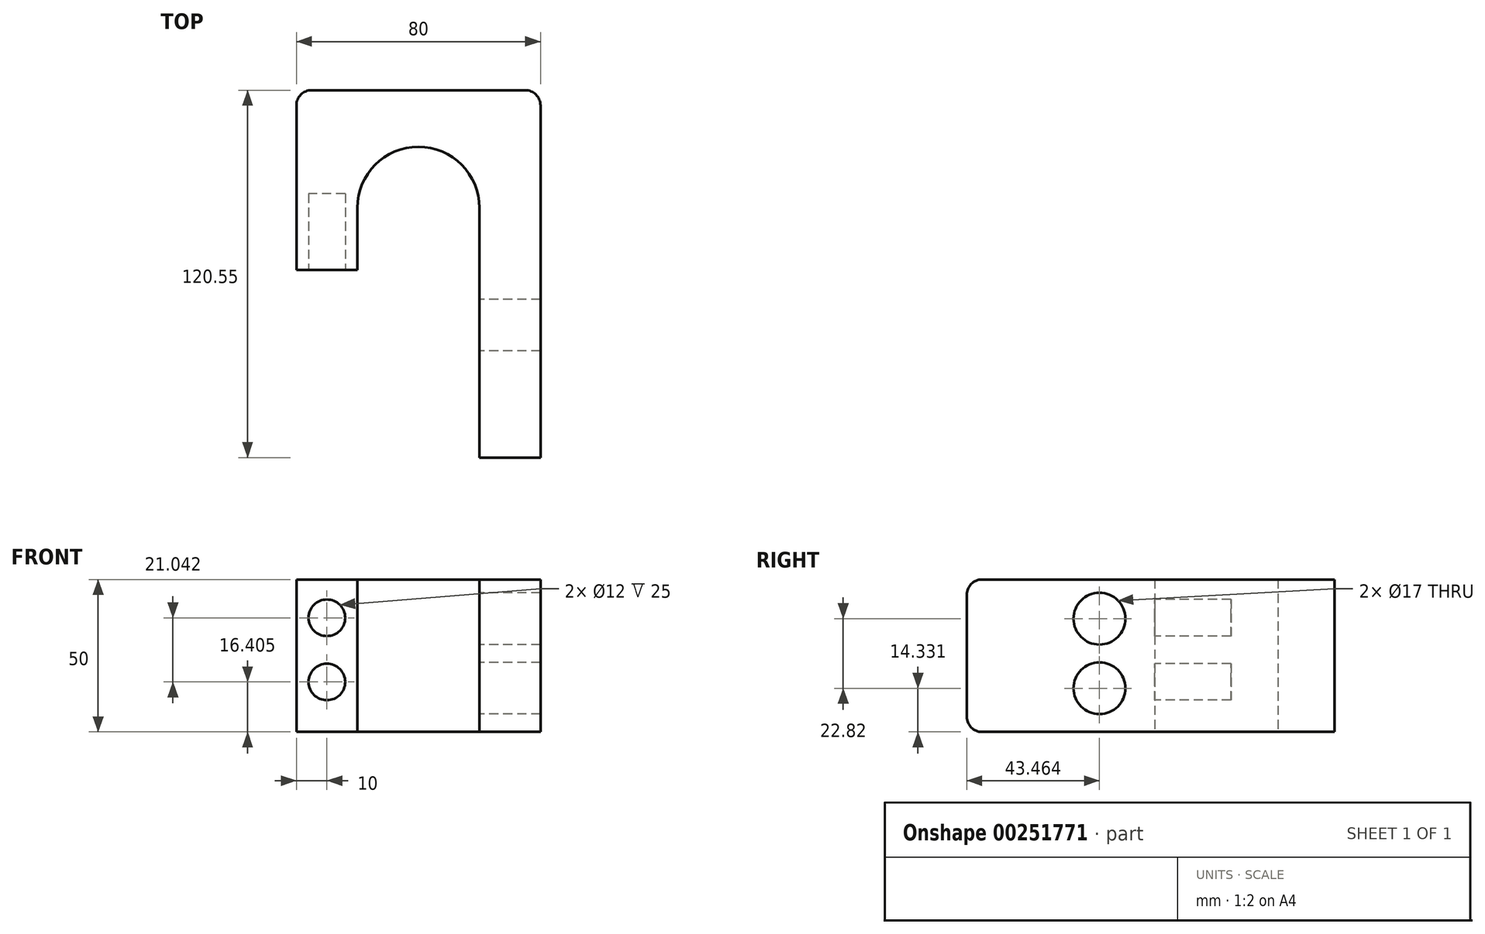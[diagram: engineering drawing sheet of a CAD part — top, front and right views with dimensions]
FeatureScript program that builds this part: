
annotation { "Feature Type Name" : "Feature", "Feature Type Description" : "" }
export const myFeature = defineFeature(function(context is Context, id is Id, definition is map)
    precondition{}
    {
        {
            var Q0;
            Q0=qCreatedBy(makeId("Top.planeOp"),FACE);
            var sketch = newSketch(context, id + "F0", { "sketchPlane" : qUnion([Q0])});
            skArc(sketch, "E0", {"start": v(20, 0) * mm, "mid": v(0, 20) * mm, "end": v(-20, 0) * mm});
            skLineSegment(sketch, "E1", {"start": v(-20, 0) * mm, "end": v(-20, -20.34) * mm});
            skLineSegment(sketch, "E2", {"start": v(-40, 38.62) * mm, "end": v(-40, -20.34) * mm});
            skLineSegment(sketch, "E3", {"start": v(-40, 38.62) * mm, "end": v(40, 38.62) * mm});
            skLineSegment(sketch, "E4", {"start": v(-20, -20.34) * mm, "end": v(-40, -20.34) * mm});
            skPoint(sketch, "E5.end.orphan", {"position": v(35.87, -52.41) * mm});
            skPoint(sketch, "E6.end.orphan", {"position": v(15.87, -52.41) * mm});
            skLineSegment(sketch, "E7", {"start": v(20, 0) * mm, "end": v(20, -81.93) * mm});
            skLineSegment(sketch, "E8", {"start": v(20, -81.93) * mm, "end": v(40, -81.93) * mm});
            skLineSegment(sketch, "E9", {"start": v(40, 38.62) * mm, "end": v(40, -81.93) * mm});
            skSolve(sketch);
        }
        {
            var Q0;
            Q0 = qSketchRegion(id + "F0", true);
            extrude(context, id + "F1", {"entities" : qUnion([Q0]), "depth" : 50 * mm});
        }
        {
            var Q0;
            Q0=makeQuery(id+"F1.opExtrude","SWEPT_EDGE",EDGE,{"disambiguationData":[OSD([sQuery(id+"F0.wireOp",EDGE,"E2"),sQuery(id+"F0.wireOp",EDGE,"E3")])]});
            var Q1;
            Q1=makeQuery(id+"F1.opExtrude","SWEPT_EDGE",EDGE,{"disambiguationData":[OSD([sQuery(id+"F0.wireOp",EDGE,"E3"),sQuery(id+"F0.wireOp",EDGE,"E9")])]});
            var Q2;
            Q2=makeQuery(id+"F1.opExtrude","CAP_EDGE",EDGE,{"disambiguationData":[OSD([sQuery(id+"F0.wireOp",EDGE,"E8")])],"isStart":false});
            var Q3;
            Q3=makeQuery(id+"F1.opExtrude","CAP_EDGE",EDGE,{"disambiguationData":[OSD([sQuery(id+"F0.wireOp",EDGE,"E8")])],"isStart":true});
            fillet(context, id + "F2", {"entities" : qUnion([Q0, Q1, Q2, Q3]), "radius" : 5 * mm, "tangentPropagation" : true, "allowEdgeOverflow" : false});
        }
        {
            var Q0;
            Q0=makeQuery(id+"F1.opExtrude","SWEPT_FACE",FACE,{"disambiguationData":[OSD([sQuery(id+"F0.wireOp",EDGE,"E7")])]});
            var sketch = newSketch(context, id + "F3", { "sketchPlane" : qUnion([Q0])});
            skCircle(sketch, "E10", {"center": v(38.47, 37.15) * mm, "radius": 8.5 * mm});
            skPoint(sketch, "E10.centerSnap0", {"position": v(38.47, 50) * mm});
            skCircle(sketch, "E11", {"center": v(38.47, 14.33) * mm, "radius": 8.5 * mm});
            skPoint(sketch, "E11.centerSnap0", {"position": v(38.47, 0) * mm});
            skSolve(sketch);
        }
        {
            var Q0;
            Q0 = qSketchRegion(id + "F3", true);
            extrude(context, id + "F4", {"entities" : qUnion([Q0]), "operationType" : NewBodyOperationType.REMOVE, "endBound" : BoundingType.THROUGH_ALL, "oppositeDirection" : true, "depth" : 25 * mm});
        }
        {
            var Q0;
            Q0=makeQuery(id+"F1.opExtrude","SWEPT_FACE",FACE,{"disambiguationData":[OSD([sQuery(id+"F0.wireOp",EDGE,"E4")])]});
            var sketch = newSketch(context, id + "F5", { "sketchPlane" : qUnion([Q0])});
            skCircle(sketch, "E12", {"center": v(-30, 37.45) * mm, "radius": 6 * mm});
            skPoint(sketch, "E12.centerSnap0", {"position": v(-30, 50) * mm});
            skCircle(sketch, "E13", {"center": v(-30, 16.4) * mm, "radius": 6 * mm});
            skPoint(sketch, "E13.centerSnap0", {"position": v(-30, 0) * mm});
            skSolve(sketch);
        }
        {
            var Q0;
            Q0 = qSketchRegion(id + "F5", true);
            extrude(context, id + "F6", {"entities" : qUnion([Q0]), "operationType" : NewBodyOperationType.REMOVE, "oppositeDirection" : true, "depth" : 25 * mm});
        }
    });
